# Revit family: Bath-Freestanding-KALLISTA-Argile-P33959
name_source: partatom
category: Plumbing Fixtures
units: mm (PartAtom-declared; Revit-internal decimal feet)

## family parameters
Cut with Voids When Loaded = No
Host = Face
OmniClass Number = 23.31.15.00
OmniClass Title = Bathtubs
Part Type = Normal
Room Calculation Point = No
Round Connector Dimension = Use Diameter
Shared = No

## types (2) — shared parameters
ADA Compliant = No
Assembly Code = D2010500
CW Connection = No
Cold Water Inlet = Cold Water Inlet
Date Modified = 12/04/2024
Default Elevation = 0"
Description = Freestanding Bathtub
Drain Included = Yes
HW Connection = No
Height = 24 3/4"
Hot Water Inlet = Hot Water Inlet
Length = 72"
Manufacturer = Kallista Co.
Master Format 2014 = 22 41 19
Master Format 2014 Name = Residential Bathtubs
Material = Lithocast
Product Name = Argile
URL = https://www.kallista.com
Vent Connection = No
Waste Connection = Yes
Waste Water Outlet = Waste Water Outlet
WaterSense Certified = No
Width = 36"

## per-type parameters (varying)
| type | Finish | Model | Type |
| HB1-Honed Black | Kallista-Lithocast-HB1-Honed_Black | P33959-00-HB1 | 1 |
| HW1-Honed White | Kallista-Lithocast-HW1-Honed_White | P33959-00-HW1 | 2 |

## geometry (parser evidence)
native form markers: Sweep x6
no freeform markers — native parametric forms only
